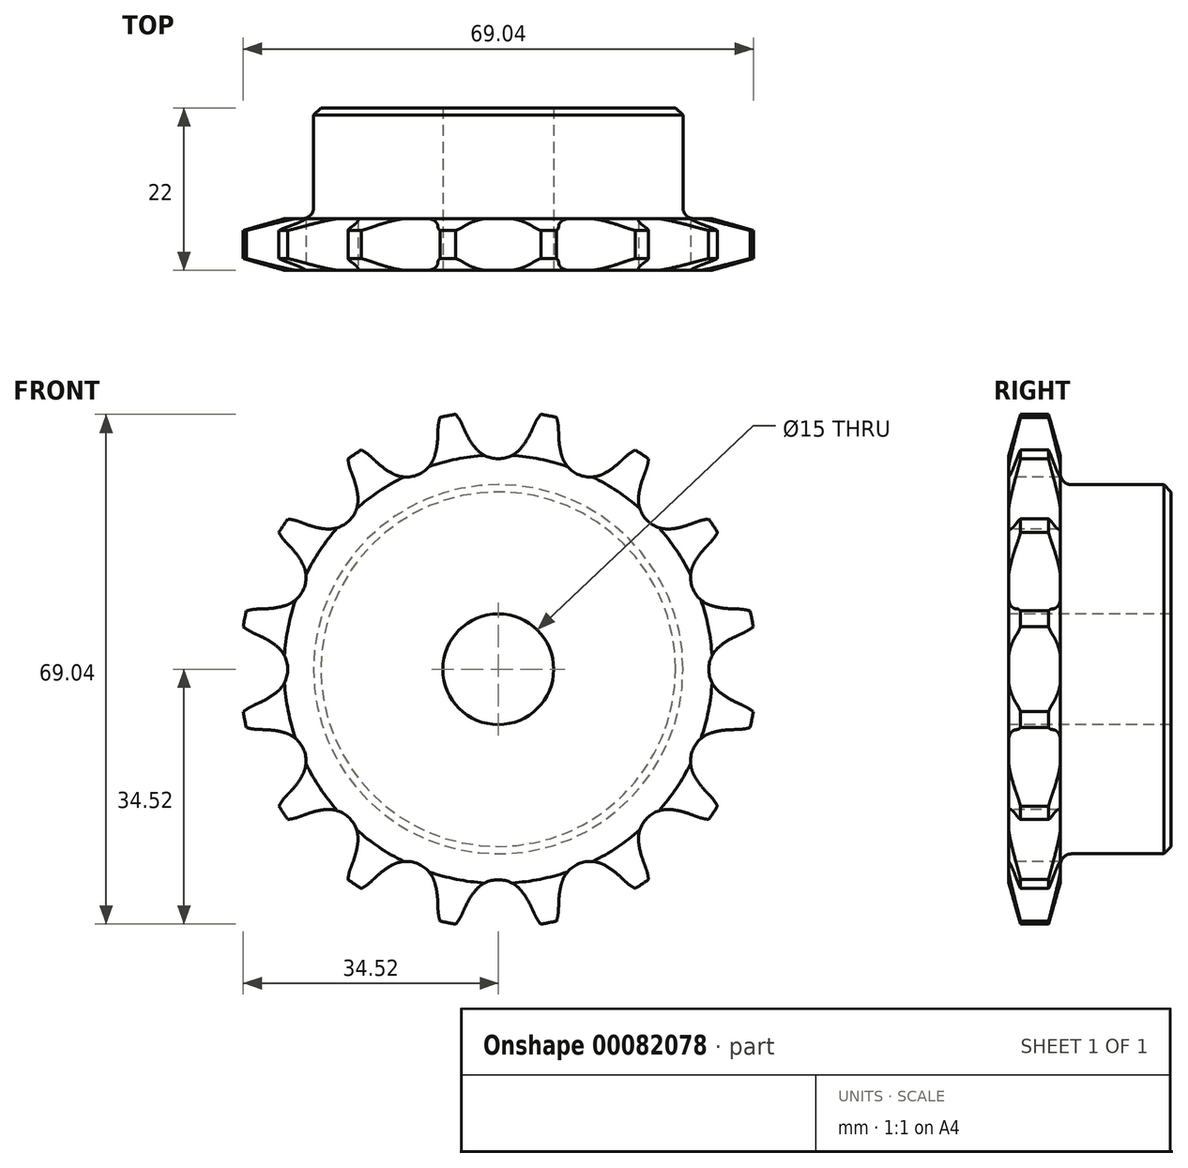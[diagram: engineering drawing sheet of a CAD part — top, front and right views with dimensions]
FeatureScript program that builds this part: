
annotation { "Feature Type Name" : "Feature", "Feature Type Description" : "" }
export const myFeature = defineFeature(function(context is Context, id is Id, definition is map)
    precondition{}
    {
        {
            var Q0;
            Q0=qCreatedBy(makeId("Right.planeOp"),FACE);
            var sketch = newSketch(context, id + "F0", { "sketchPlane" : qUnion([Q0])});
            skLineSegment(sketch, "E0", {"start": v(-9.83, 0) * mm, "end": v(12.17, 0) * mm, "construction": true});
            skLineSegment(sketch, "E1.bottom", {"start": v(-9.83, 7.5) * mm, "end": v(12.17, 7.5) * mm});
            skLineSegment(sketch, "E1.top", {"start": v(-9.83, 25) * mm, "end": v(12.17, 25) * mm});
            skLineSegment(sketch, "E1.left", {"start": v(-9.83, 7.5) * mm, "end": v(-9.83, 25) * mm, "construction": true});
            skLineSegment(sketch, "E1.right", {"start": v(12.17, 7.5) * mm, "end": v(12.17, 25) * mm});
            skLineSegment(sketch, "E2.bottom", {"start": v(-9.83, 7.5) * mm, "end": v(-2.83, 7.5) * mm, "construction": true});
            skLineSegment(sketch, "E2.top", {"start": v(-9.83, 35) * mm, "end": v(-2.83, 35) * mm});
            skLineSegment(sketch, "E2.left", {"start": v(-9.83, 7.5) * mm, "end": v(-9.83, 35) * mm});
            skLineSegment(sketch, "E2.right", {"start": v(-2.83, 7.5) * mm, "end": v(-2.83, 35) * mm});
            skLineSegment(sketch, "E3.MirrorCS", {"start": v(-9.83, -7.5) * mm, "end": v(-9.83, -25) * mm, "construction": true});
            skLineSegment(sketch, "E4.MirrorCS", {"start": v(-9.83, -7.5) * mm, "end": v(12.17, -7.5) * mm});
            skLineSegment(sketch, "E5.MirrorCS", {"start": v(-2.83, -7.5) * mm, "end": v(-2.83, -35) * mm});
            skLineSegment(sketch, "E6.MirrorCS", {"start": v(-9.83, -25) * mm, "end": v(12.17, -25) * mm});
            skLineSegment(sketch, "E7.MirrorCS", {"start": v(-9.83, -35) * mm, "end": v(-2.83, -35) * mm});
            skLineSegment(sketch, "E8.MirrorCS", {"start": v(12.17, -7.5) * mm, "end": v(12.17, -25) * mm});
            skLineSegment(sketch, "E9.MirrorCS", {"start": v(-9.83, -7.5) * mm, "end": v(-9.83, -35) * mm});
            skLineSegment(sketch, "E10.MirrorCS", {"start": v(-9.83, -7.5) * mm, "end": v(-2.83, -7.5) * mm, "construction": true});
            skSolve(sketch);
        }
        {
            var Q0;
            {var subQ5=sQuery(id+"F0.wireOp",EDGE,"E2.top");Q0=makeQuery(id+"F0.imprint","IMPRINT",FACE,{"disambiguationData":[TD([[makeQuery(id+"F0.imprint","IMPRINT",EDGE,{"derivedFrom":subQ5}),-1.0]])]});}
            var Q1;
            {var subQ0=sQuery(id+"F0.wireOp",EDGE,"E2.left");var subQ1=sQuery(id+"F0.wireOp",EDGE,"E1.bottom");var subQ2=makeQuery(id+"F0.imprint","INTERSECT",VERTEX,{"derivedFrom":[subQ1,subQ0]});Q1=makeQuery(id+"F0.imprint","IMPRINT",FACE,{"disambiguationData":[TD([[makeQuery(id+"F0.imprint","IMPRINT",EDGE,{"disambiguationData":[TD([[subQ2,-1.0]])],"derivedFrom":subQ1}),1.0]])]});}
            var Q2;
            {var subQ0=sQuery(id+"F0.wireOp",EDGE,"E1.right");Q2=makeQuery(id+"F0.imprint","IMPRINT",FACE,{"disambiguationData":[TD([[makeQuery(id+"F0.imprint","IMPRINT",EDGE,{"derivedFrom":subQ0}),1.0]])]});}
            var Q3;
            Q3=sQuery(id+"F0.wireOp",EDGE,"E0");
            revolve(context, id + "F1", {"entities" : qUnion([Q0, Q1, Q2]), "axis" : qUnion([Q3]), "revolveType" : RevolveType.FULL});
        }
        {
            var Q0;
            Q0=makeQuery(id+"F1.opRevolve","SWEPT_EDGE",EDGE,{"disambiguationData":[OSD([sQuery(id+"F0.wireOp",EDGE,"E1.top"),sQuery(id+"F0.wireOp",EDGE,"E2.right")])]});
            fillet(context, id + "F2", {"entities" : qUnion([Q0]), "radius" : 1.5 * mm, "tangentPropagation" : true, "allowEdgeOverflow" : false});
        }
        {
            var Q0;
            Q0=makeQuery(id+"F1.opRevolve","SWEPT_EDGE",EDGE,{"disambiguationData":[OSD([sQuery(id+"F0.wireOp",EDGE,"E1.top"),sQuery(id+"F0.wireOp",EDGE,"E1.right")])]});
            chamfer(context, id + "F3", {"entities" : qUnion([Q0]), "width" : 1 * mm, "tangentPropagation" : true});
        }
        {
            var Q0;
            Q0=makeQuery(id+"F1.opRevolve","SWEPT_EDGE",EDGE,{"disambiguationData":[OSD([sQuery(id+"F0.wireOp",EDGE,"E2.top"),sQuery(id+"F0.wireOp",EDGE,"E2.left")])]});
            var Q1;
            Q1=makeQuery(id+"F1.opRevolve","SWEPT_EDGE",EDGE,{"disambiguationData":[OSD([sQuery(id+"F0.wireOp",EDGE,"E2.top"),sQuery(id+"F0.wireOp",EDGE,"E2.right")])]});
            chamfer(context, id + "F4", {"entities" : qUnion([Q0, Q1]), "chamferType" : ChamferType.TWO_OFFSETS, "width1" : 6 * mm, "oppositeDirection" : false, "width2" : 1.6 * mm, "tangentPropagation" : true});
        }
        {
            var Q0;
            Q0=makeQuery(id+"F1.opRevolve","SWEPT_FACE",FACE,{"disambiguationData":[OSD([sQuery(id+"F0.wireOp",EDGE,"E2.left")])]});
            var sketch = newSketch(context, id + "F5", { "sketchPlane" : qUnion([Q0])});
            skCircle(sketch, "E11", {"center": v(0, 0) * mm, "radius": 32.5 * mm, "construction": true});
            skLineSegment(sketch, "E12", {"start": v(0, 0) * mm, "end": v(0, 32.5) * mm, "construction": true});
            skLineSegment(sketch, "E13", {"start": v(0, 32.5) * mm, "end": v(33.37, 32.5) * mm, "construction": true});
            skLineSegment(sketch, "E14", {"start": v(0, 32.5) * mm, "end": v(4.95, 36.47) * mm, "construction": true});
            skLineSegment(sketch, "E15", {"start": v(4.95, 36.47) * mm, "end": v(-4.48, 32.22) * mm, "construction": true});
            skLineSegment(sketch, "E16", {"start": v(3.87, 13.68) * mm, "end": v(-4.48, 32.22) * mm, "construction": true});
            skLineSegment(sketch, "E17", {"start": v(0, 0) * mm, "end": v(-7.12, 35.79) * mm, "construction": true});
            skArc(sketch, "E18", {"start": v(-7.12, 35.79) * mm, "mid": v(-15.88, 26.2) * mm, "end": v(-4.87, 33.1) * mm, "construction": true});
            skArc(sketch, "E19", {"start": v(-4.87, 33.1) * mm, "mid": v(-5.81, 34.6) * mm, "end": v(-7.12, 35.79) * mm});
            skLineSegment(sketch, "E20", {"start": v(-4.48, 32.22) * mm, "end": v(-4.48, 32.22) * mm});
            skArc(sketch, "E21", {"start": v(-3.12, 30) * mm, "mid": v(13.78, 41.88) * mm, "end": v(-4.48, 32.22) * mm, "construction": true});
            skArc(sketch, "E22", {"start": v(-4.48, 32.22) * mm, "mid": v(-3.87, 31.07) * mm, "end": v(-3.12, 30) * mm});
            skArc(sketch, "E23.MirrorCS", {"start": v(4.48, 32.22) * mm, "mid": v(3.87, 31.07) * mm, "end": v(3.12, 30) * mm});
            skArc(sketch, "E24.MirrorCS", {"start": v(4.87, 33.1) * mm, "mid": v(5.81, 34.6) * mm, "end": v(7.12, 35.79) * mm});
            skLineSegment(sketch, "E25.MirrorCS", {"start": v(-3.87, 13.68) * mm, "end": v(4.48, 32.22) * mm, "construction": true});
            skArc(sketch, "E26", {"start": v(-3.12, 30) * mm, "mid": v(0, 28.5) * mm, "end": v(3.12, 30) * mm});
            skArc(sketch, "E27", {"start": v(3.12, 30) * mm, "mid": v(0, 36.5) * mm, "end": v(-3.12, 30) * mm, "construction": true});
            skLineSegment(sketch, "E28", {"start": v(4.87, 33.1) * mm, "end": v(4.48, 32.22) * mm});
            skLineSegment(sketch, "E29", {"start": v(-4.87, 33.1) * mm, "end": v(-4.48, 32.22) * mm});
            skArc(sketch, "E30.1.0", {"start": v(-17.17, 28.7) * mm, "mid": v(-18.6, 29.73) * mm, "end": v(-20.27, 30.34) * mm});
            skLineSegment(sketch, "E30.1.1", {"start": v(-17.17, 28.7) * mm, "end": v(-16.47, 28.05) * mm});
            skArc(sketch, "E30.1.2", {"start": v(-16.47, 28.05) * mm, "mid": v(-15.47, 27.22) * mm, "end": v(-14.36, 26.52) * mm});
            skArc(sketch, "E30.1.3", {"start": v(-14.36, 26.52) * mm, "mid": v(-10.9, 26.33) * mm, "end": v(-8.6, 28.9) * mm});
            skArc(sketch, "E30.1.4", {"start": v(-8.19, 31.49) * mm, "mid": v(-8.31, 30.18) * mm, "end": v(-8.6, 28.9) * mm});
            skLineSegment(sketch, "E30.1.5", {"start": v(-8.16, 32.44) * mm, "end": v(-8.19, 31.49) * mm});
            skArc(sketch, "E30.1.6", {"start": v(-8.16, 32.44) * mm, "mid": v(-7.87, 34.18) * mm, "end": v(-7.12, 35.79) * mm});
            skArc(sketch, "E30.2.0", {"start": v(-26.85, 19.95) * mm, "mid": v(-28.57, 20.35) * mm, "end": v(-30.34, 20.27) * mm});
            skLineSegment(sketch, "E30.2.1", {"start": v(-26.85, 19.95) * mm, "end": v(-25.96, 19.61) * mm});
            skArc(sketch, "E30.2.2", {"start": v(-25.96, 19.61) * mm, "mid": v(-24.7, 19.23) * mm, "end": v(-23.42, 19) * mm});
            skArc(sketch, "E30.2.3", {"start": v(-23.42, 19) * mm, "mid": v(-20.15, 20.15) * mm, "end": v(-19, 23.42) * mm});
            skArc(sketch, "E30.2.4", {"start": v(-19.61, 25.96) * mm, "mid": v(-19.23, 24.7) * mm, "end": v(-19, 23.42) * mm});
            skLineSegment(sketch, "E30.2.5", {"start": v(-19.95, 26.85) * mm, "end": v(-19.61, 25.96) * mm});
            skArc(sketch, "E30.2.6", {"start": v(-19.95, 26.85) * mm, "mid": v(-20.35, 28.57) * mm, "end": v(-20.27, 30.34) * mm});
            skArc(sketch, "E31.1.3.0", {"start": v(-32.44, 8.16) * mm, "mid": v(-34.18, 7.87) * mm, "end": v(-35.79, 7.12) * mm});
            skLineSegment(sketch, "E31.4.3.0", {"start": v(-32.44, 8.16) * mm, "end": v(-31.49, 8.19) * mm});
            skArc(sketch, "E31.7.3.0", {"start": v(-31.49, 8.19) * mm, "mid": v(-30.18, 8.31) * mm, "end": v(-28.9, 8.6) * mm});
            skArc(sketch, "E31.11.3.0", {"start": v(-28.9, 8.6) * mm, "mid": v(-26.33, 10.9) * mm, "end": v(-26.52, 14.36) * mm});
            skArc(sketch, "E31.15.3.0", {"start": v(-28.05, 16.47) * mm, "mid": v(-27.22, 15.47) * mm, "end": v(-26.52, 14.36) * mm});
            skLineSegment(sketch, "E31.19.3.0", {"start": v(-28.7, 17.17) * mm, "end": v(-28.05, 16.47) * mm});
            skArc(sketch, "E31.22.3.0", {"start": v(-28.7, 17.17) * mm, "mid": v(-29.73, 18.6) * mm, "end": v(-30.34, 20.27) * mm});
            skArc(sketch, "E31.1.4.0", {"start": v(-33.1, -4.87) * mm, "mid": v(-34.6, -5.81) * mm, "end": v(-35.79, -7.12) * mm});
            skLineSegment(sketch, "E31.4.4.0", {"start": v(-33.1, -4.87) * mm, "end": v(-32.22, -4.48) * mm});
            skArc(sketch, "E31.7.4.0", {"start": v(-32.22, -4.48) * mm, "mid": v(-31.07, -3.87) * mm, "end": v(-30, -3.12) * mm});
            skArc(sketch, "E31.11.4.0", {"start": v(-30, -3.12) * mm, "mid": v(-28.5, 0) * mm, "end": v(-30, 3.12) * mm});
            skArc(sketch, "E31.15.4.0", {"start": v(-32.22, 4.48) * mm, "mid": v(-31.07, 3.87) * mm, "end": v(-30, 3.12) * mm});
            skLineSegment(sketch, "E31.19.4.0", {"start": v(-33.1, 4.87) * mm, "end": v(-32.22, 4.48) * mm});
            skArc(sketch, "E31.22.4.0", {"start": v(-33.1, 4.87) * mm, "mid": v(-34.6, 5.81) * mm, "end": v(-35.79, 7.12) * mm});
            skArc(sketch, "E31.1.5.0", {"start": v(-28.7, -17.17) * mm, "mid": v(-29.73, -18.6) * mm, "end": v(-30.34, -20.27) * mm});
            skLineSegment(sketch, "E31.4.5.0", {"start": v(-28.7, -17.17) * mm, "end": v(-28.05, -16.47) * mm});
            skArc(sketch, "E31.7.5.0", {"start": v(-28.05, -16.47) * mm, "mid": v(-27.22, -15.47) * mm, "end": v(-26.52, -14.36) * mm});
            skArc(sketch, "E31.11.5.0", {"start": v(-26.52, -14.36) * mm, "mid": v(-26.33, -10.9) * mm, "end": v(-28.9, -8.6) * mm});
            skArc(sketch, "E31.15.5.0", {"start": v(-31.49, -8.19) * mm, "mid": v(-30.18, -8.31) * mm, "end": v(-28.9, -8.6) * mm});
            skLineSegment(sketch, "E31.19.5.0", {"start": v(-32.44, -8.16) * mm, "end": v(-31.49, -8.19) * mm});
            skArc(sketch, "E31.22.5.0", {"start": v(-32.44, -8.16) * mm, "mid": v(-34.18, -7.87) * mm, "end": v(-35.79, -7.12) * mm});
            skArc(sketch, "E31.1.6.0", {"start": v(-19.95, -26.85) * mm, "mid": v(-20.35, -28.57) * mm, "end": v(-20.27, -30.34) * mm});
            skLineSegment(sketch, "E31.4.6.0", {"start": v(-19.95, -26.85) * mm, "end": v(-19.61, -25.96) * mm});
            skArc(sketch, "E31.7.6.0", {"start": v(-19.61, -25.96) * mm, "mid": v(-19.23, -24.7) * mm, "end": v(-19, -23.42) * mm});
            skArc(sketch, "E31.11.6.0", {"start": v(-19, -23.42) * mm, "mid": v(-20.15, -20.15) * mm, "end": v(-23.42, -19) * mm});
            skArc(sketch, "E31.15.6.0", {"start": v(-25.96, -19.61) * mm, "mid": v(-24.7, -19.23) * mm, "end": v(-23.42, -19) * mm});
            skLineSegment(sketch, "E31.19.6.0", {"start": v(-26.85, -19.95) * mm, "end": v(-25.96, -19.61) * mm});
            skArc(sketch, "E31.22.6.0", {"start": v(-26.85, -19.95) * mm, "mid": v(-28.57, -20.35) * mm, "end": v(-30.34, -20.27) * mm});
            skArc(sketch, "E31.1.7.0", {"start": v(-8.16, -32.44) * mm, "mid": v(-7.87, -34.18) * mm, "end": v(-7.12, -35.79) * mm});
            skLineSegment(sketch, "E31.4.7.0", {"start": v(-8.16, -32.44) * mm, "end": v(-8.19, -31.49) * mm});
            skArc(sketch, "E31.7.7.0", {"start": v(-8.19, -31.49) * mm, "mid": v(-8.31, -30.18) * mm, "end": v(-8.6, -28.9) * mm});
            skArc(sketch, "E31.11.7.0", {"start": v(-8.6, -28.9) * mm, "mid": v(-10.9, -26.33) * mm, "end": v(-14.36, -26.52) * mm});
            skArc(sketch, "E31.15.7.0", {"start": v(-16.47, -28.05) * mm, "mid": v(-15.47, -27.22) * mm, "end": v(-14.36, -26.52) * mm});
            skLineSegment(sketch, "E31.19.7.0", {"start": v(-17.17, -28.7) * mm, "end": v(-16.47, -28.05) * mm});
            skArc(sketch, "E31.22.7.0", {"start": v(-17.17, -28.7) * mm, "mid": v(-18.6, -29.73) * mm, "end": v(-20.27, -30.34) * mm});
            skArc(sketch, "E31.1.8.0", {"start": v(4.87, -33.1) * mm, "mid": v(5.81, -34.6) * mm, "end": v(7.12, -35.79) * mm});
            skLineSegment(sketch, "E31.4.8.0", {"start": v(4.87, -33.1) * mm, "end": v(4.48, -32.22) * mm});
            skArc(sketch, "E31.7.8.0", {"start": v(4.48, -32.22) * mm, "mid": v(3.87, -31.07) * mm, "end": v(3.12, -30) * mm});
            skArc(sketch, "E31.11.8.0", {"start": v(3.12, -30) * mm, "mid": v(0, -28.5) * mm, "end": v(-3.12, -30) * mm});
            skArc(sketch, "E31.15.8.0", {"start": v(-4.48, -32.22) * mm, "mid": v(-3.87, -31.07) * mm, "end": v(-3.12, -30) * mm});
            skLineSegment(sketch, "E31.19.8.0", {"start": v(-4.87, -33.1) * mm, "end": v(-4.48, -32.22) * mm});
            skArc(sketch, "E31.22.8.0", {"start": v(-4.87, -33.1) * mm, "mid": v(-5.81, -34.6) * mm, "end": v(-7.12, -35.79) * mm});
            skArc(sketch, "E31.1.9.0", {"start": v(17.17, -28.7) * mm, "mid": v(18.6, -29.73) * mm, "end": v(20.27, -30.34) * mm});
            skLineSegment(sketch, "E31.4.9.0", {"start": v(17.17, -28.7) * mm, "end": v(16.47, -28.05) * mm});
            skArc(sketch, "E31.7.9.0", {"start": v(16.47, -28.05) * mm, "mid": v(15.47, -27.22) * mm, "end": v(14.36, -26.52) * mm});
            skArc(sketch, "E31.11.9.0", {"start": v(14.36, -26.52) * mm, "mid": v(10.9, -26.33) * mm, "end": v(8.6, -28.9) * mm});
            skArc(sketch, "E31.15.9.0", {"start": v(8.19, -31.49) * mm, "mid": v(8.31, -30.18) * mm, "end": v(8.6, -28.9) * mm});
            skLineSegment(sketch, "E31.19.9.0", {"start": v(8.16, -32.44) * mm, "end": v(8.19, -31.49) * mm});
            skArc(sketch, "E31.22.9.0", {"start": v(8.16, -32.44) * mm, "mid": v(7.87, -34.18) * mm, "end": v(7.12, -35.79) * mm});
            skArc(sketch, "E31.1.10.0", {"start": v(26.85, -19.95) * mm, "mid": v(28.57, -20.35) * mm, "end": v(30.34, -20.27) * mm});
            skLineSegment(sketch, "E31.4.10.0", {"start": v(26.85, -19.95) * mm, "end": v(25.96, -19.61) * mm});
            skArc(sketch, "E31.7.10.0", {"start": v(25.96, -19.61) * mm, "mid": v(24.7, -19.23) * mm, "end": v(23.42, -19) * mm});
            skArc(sketch, "E31.11.10.0", {"start": v(23.42, -19) * mm, "mid": v(20.15, -20.15) * mm, "end": v(19, -23.42) * mm});
            skArc(sketch, "E31.15.10.0", {"start": v(19.61, -25.96) * mm, "mid": v(19.23, -24.7) * mm, "end": v(19, -23.42) * mm});
            skLineSegment(sketch, "E31.19.10.0", {"start": v(19.95, -26.85) * mm, "end": v(19.61, -25.96) * mm});
            skArc(sketch, "E31.22.10.0", {"start": v(19.95, -26.85) * mm, "mid": v(20.35, -28.57) * mm, "end": v(20.27, -30.34) * mm});
            skArc(sketch, "E31.1.11.0", {"start": v(32.44, -8.16) * mm, "mid": v(34.18, -7.87) * mm, "end": v(35.79, -7.12) * mm});
            skLineSegment(sketch, "E31.4.11.0", {"start": v(32.44, -8.16) * mm, "end": v(31.49, -8.19) * mm});
            skArc(sketch, "E31.7.11.0", {"start": v(31.49, -8.19) * mm, "mid": v(30.18, -8.31) * mm, "end": v(28.9, -8.6) * mm});
            skArc(sketch, "E31.11.11.0", {"start": v(28.9, -8.6) * mm, "mid": v(26.33, -10.9) * mm, "end": v(26.52, -14.36) * mm});
            skArc(sketch, "E31.15.11.0", {"start": v(28.05, -16.47) * mm, "mid": v(27.22, -15.47) * mm, "end": v(26.52, -14.36) * mm});
            skLineSegment(sketch, "E31.19.11.0", {"start": v(28.7, -17.17) * mm, "end": v(28.05, -16.47) * mm});
            skArc(sketch, "E31.22.11.0", {"start": v(28.7, -17.17) * mm, "mid": v(29.73, -18.6) * mm, "end": v(30.34, -20.27) * mm});
            skArc(sketch, "E31.1.12.0", {"start": v(33.1, 4.87) * mm, "mid": v(34.6, 5.81) * mm, "end": v(35.79, 7.12) * mm});
            skLineSegment(sketch, "E31.4.12.0", {"start": v(33.1, 4.87) * mm, "end": v(32.22, 4.48) * mm});
            skArc(sketch, "E31.7.12.0", {"start": v(32.22, 4.48) * mm, "mid": v(31.07, 3.87) * mm, "end": v(30, 3.12) * mm});
            skArc(sketch, "E31.11.12.0", {"start": v(30, 3.12) * mm, "mid": v(28.5, 0) * mm, "end": v(30, -3.12) * mm});
            skArc(sketch, "E31.15.12.0", {"start": v(32.22, -4.48) * mm, "mid": v(31.07, -3.87) * mm, "end": v(30, -3.12) * mm});
            skLineSegment(sketch, "E31.19.12.0", {"start": v(33.1, -4.87) * mm, "end": v(32.22, -4.48) * mm});
            skArc(sketch, "E31.22.12.0", {"start": v(33.1, -4.87) * mm, "mid": v(34.6, -5.81) * mm, "end": v(35.79, -7.12) * mm});
            skArc(sketch, "E31.1.13.0", {"start": v(28.7, 17.17) * mm, "mid": v(29.73, 18.6) * mm, "end": v(30.34, 20.27) * mm});
            skLineSegment(sketch, "E31.4.13.0", {"start": v(28.7, 17.17) * mm, "end": v(28.05, 16.47) * mm});
            skArc(sketch, "E31.7.13.0", {"start": v(28.05, 16.47) * mm, "mid": v(27.22, 15.47) * mm, "end": v(26.52, 14.36) * mm});
            skArc(sketch, "E31.11.13.0", {"start": v(26.52, 14.36) * mm, "mid": v(26.33, 10.9) * mm, "end": v(28.9, 8.6) * mm});
            skArc(sketch, "E31.15.13.0", {"start": v(31.49, 8.19) * mm, "mid": v(30.18, 8.31) * mm, "end": v(28.9, 8.6) * mm});
            skLineSegment(sketch, "E31.19.13.0", {"start": v(32.44, 8.16) * mm, "end": v(31.49, 8.19) * mm});
            skArc(sketch, "E31.22.13.0", {"start": v(32.44, 8.16) * mm, "mid": v(34.18, 7.87) * mm, "end": v(35.79, 7.12) * mm});
            skArc(sketch, "E31.1.14.0", {"start": v(19.95, 26.85) * mm, "mid": v(20.35, 28.57) * mm, "end": v(20.27, 30.34) * mm});
            skLineSegment(sketch, "E31.4.14.0", {"start": v(19.95, 26.85) * mm, "end": v(19.61, 25.96) * mm});
            skArc(sketch, "E31.7.14.0", {"start": v(19.61, 25.96) * mm, "mid": v(19.23, 24.7) * mm, "end": v(19, 23.42) * mm});
            skArc(sketch, "E31.11.14.0", {"start": v(19, 23.42) * mm, "mid": v(20.15, 20.15) * mm, "end": v(23.42, 19) * mm});
            skArc(sketch, "E31.15.14.0", {"start": v(25.96, 19.61) * mm, "mid": v(24.7, 19.23) * mm, "end": v(23.42, 19) * mm});
            skLineSegment(sketch, "E31.19.14.0", {"start": v(26.85, 19.95) * mm, "end": v(25.96, 19.61) * mm});
            skArc(sketch, "E31.22.14.0", {"start": v(26.85, 19.95) * mm, "mid": v(28.57, 20.35) * mm, "end": v(30.34, 20.27) * mm});
            skArc(sketch, "E31.1.15.0", {"start": v(8.16, 32.44) * mm, "mid": v(7.87, 34.18) * mm, "end": v(7.12, 35.79) * mm});
            skLineSegment(sketch, "E31.4.15.0", {"start": v(8.16, 32.44) * mm, "end": v(8.19, 31.49) * mm});
            skArc(sketch, "E31.7.15.0", {"start": v(8.19, 31.49) * mm, "mid": v(8.31, 30.18) * mm, "end": v(8.6, 28.9) * mm});
            skArc(sketch, "E31.11.15.0", {"start": v(8.6, 28.9) * mm, "mid": v(10.9, 26.33) * mm, "end": v(14.36, 26.52) * mm});
            skArc(sketch, "E31.15.15.0", {"start": v(16.47, 28.05) * mm, "mid": v(15.47, 27.22) * mm, "end": v(14.36, 26.52) * mm});
            skLineSegment(sketch, "E31.19.15.0", {"start": v(17.17, 28.7) * mm, "end": v(16.47, 28.05) * mm});
            skArc(sketch, "E31.22.15.0", {"start": v(17.17, 28.7) * mm, "mid": v(18.6, 29.73) * mm, "end": v(20.27, 30.34) * mm});
            skSolve(sketch);
        }
        {
            var Q0;
            Q0 = qSketchRegion(id + "F5", true);
            extrude(context, id + "F6", {"entities" : qUnion([Q0]), "operationType" : NewBodyOperationType.INTERSECT, "oppositeDirection" : true, "depth" : 25 * mm});
        }
    });
